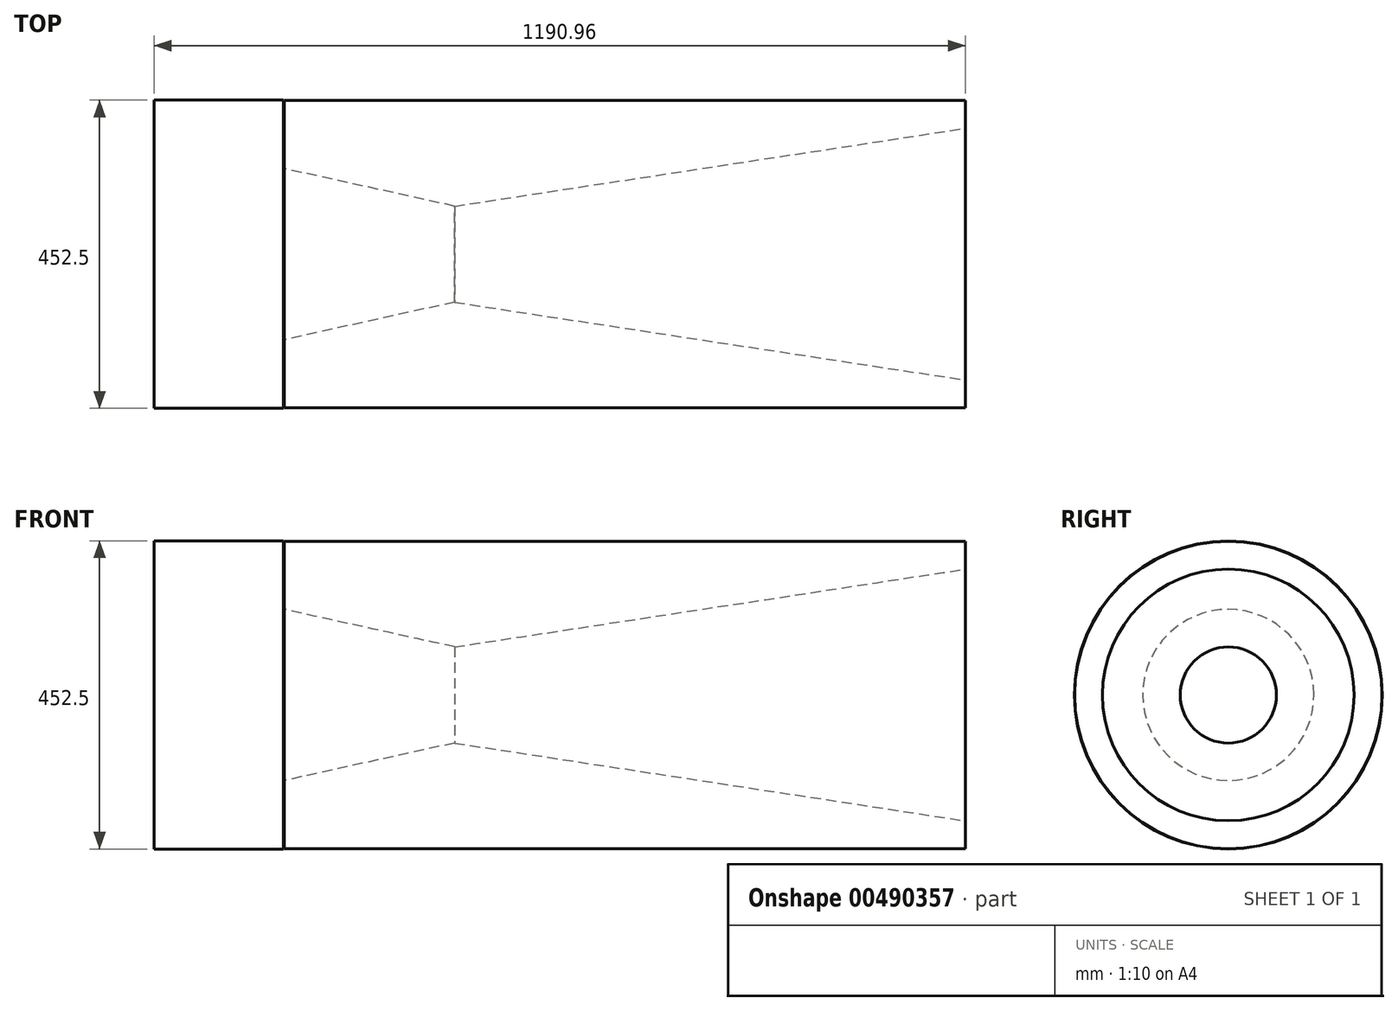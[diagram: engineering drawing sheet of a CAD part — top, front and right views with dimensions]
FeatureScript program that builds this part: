
annotation { "Feature Type Name" : "Feature", "Feature Type Description" : "" }
export const myFeature = defineFeature(function(context is Context, id is Id, definition is map)
    precondition{}
    {
        {
            var Q0;
            Q0=qCreatedBy(makeId("Front.planeOp"),FACE);
            var sketch = newSketch(context, id + "F0", { "sketchPlane" : qUnion([Q0])});
            skLineSegment(sketch, "E0", {"start": v(-250, -125.67) * mm, "end": v(0, -70.56) * mm});
            skLineSegment(sketch, "E1", {"start": v(0, -70.56) * mm, "end": v(750, -184.81) * mm});
            skLineSegment(sketch, "E2", {"start": v(750, -184.81) * mm, "end": v(750, -225.67) * mm});
            skLineSegment(sketch, "E3", {"start": v(750, -225.67) * mm, "end": v(-250, -225.67) * mm});
            skLineSegment(sketch, "E4", {"start": v(-250, -225.67) * mm, "end": v(-250, -125.67) * mm});
            skLineSegment(sketch, "E5", {"start": v(-250, -125.67) * mm, "end": v(-250, -125.67) * mm});
            skLineSegment(sketch, "E6", {"start": v(-212.83, 0) * mm, "end": v(205.65, 0) * mm});
            skLineSegment(sketch, "E7.bottom", {"start": v(-250.96, 0) * mm, "end": v(-440.96, 0) * mm});
            skLineSegment(sketch, "E7.top", {"start": v(-250.96, -226.25) * mm, "end": v(-440.96, -226.25) * mm});
            skLineSegment(sketch, "E7.left", {"start": v(-250.96, 0) * mm, "end": v(-250.96, -226.25) * mm});
            skLineSegment(sketch, "E7.right", {"start": v(-440.96, 0) * mm, "end": v(-440.96, -226.25) * mm});
            skSolve(sketch);
        }
        {
            var Q0;
            Q0=makeQuery(id+"F0.imprint","IMPRINT",FACE,{"disambiguationData":[TD([[makeQuery(id+"F0.imprint","IMPRINT",EDGE,{"derivedFrom":sQuery(id+"F0.wireOp",EDGE,"E0")}),-1.0]])]});
            var Q1;
            Q1=sQuery(id+"F0.wireOp",EDGE,"E6");
            revolve(context, id + "F1", {"entities" : qUnion([Q0]), "axis" : qUnion([Q1]), "revolveType" : RevolveType.FULL});
        }
        {
            var Q0;
            Q0=makeQuery(id+"F0.imprint","IMPRINT",FACE,{"disambiguationData":[TD([[makeQuery(id+"F0.imprint","IMPRINT",EDGE,{"derivedFrom":sQuery(id+"F0.wireOp",EDGE,"E7.bottom")}),1.0]])]});
            var Q1;
            Q1=sQuery(id+"F0.wireOp",EDGE,"E6");
            revolve(context, id + "F2", {"entities" : qUnion([Q0]), "axis" : qUnion([Q1]), "revolveType" : RevolveType.FULL});
        }
    });
